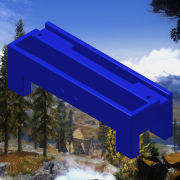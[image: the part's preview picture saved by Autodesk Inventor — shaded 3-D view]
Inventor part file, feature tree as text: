
AUTODESK INVENTOR PART (.ipt)
format: ipt  version: 2015 SP1 (Build 190203100, 203)  size: 321,536 bytes
history: native  units: in
note: dims shown in document units (in); Inventor stores cm internally (conversion verified against a paired STEP export)
features: sketch x11, extrude x7, hole x3, reference x2, fillet x1, projected_geometry x1
ambient origin geometry x8: Origin, YZ Plane, XZ Plane, XY Plane, X Axis, Y Axis, Z Axis, Center Point
bodies: Solid1 (feature_tree)
feature tree (25):
  extrude  "Extrusion1"  Depth=1.25in
  extrude  "Extrusion2"  Depth=2.5in TaperAngle=0.0deg
  extrude  "Extrusion3"  Depth=1.0in
  extrude  "Extrusion4"  Depth=1.0in
  extrude  "Extrusion5"  Depth=0.5in
  extrude  "Extrusion6"  Depth=0.5in
  sketch  "Sketch9"  dims[d13=1.0in d14=0.0in d15=3.8in]
  hole  "Hole1"  [1 undecoded]
  hole  "Hole2"  [1 undecoded]
  extrude  "Extrusion7"  Depth=7.0in
  hole  "Hole3"  [1 undecoded]
  fillet  "Fillet1"  Radius=0.75in
  sketch  "Sketch1"  dims[d0=7.5in d1=1.25in]
  sketch  "Sketch3"  dims[d2=7.5in d3=2.5in d4=0.0in]
  sketch  "Sketch4"  dims[d5=1.0in d6=1.0in]
  sketch  "Sketch5"  dims[d7=1.0in d8=1.0in]
  sketch  "Sketch6"  dims[d9=0.5in d10=0.5in]
  sketch  "Sketch8"  dims[d11=0.5in d12=0.5in]
  sketch  "Sketch10"  dims[d16=1.85in d17=1.0in d18=0.0in]
  reference  "Reference1"
  sketch  "Sketch11"  dims[d22=1.0in d23=0.0in d24=7.0in]
  reference  "Reference2"
  sketch  "Sketch12"  dims[d26=1.0in d27=0.0in d28=0.5in d29=0.75in]
  sketch  "Sketch13"  dims[d30=3.125in d34=0.525in d35=1.125in d36=2.9375in d37=0.211in d38=1.0in d39=0.0in d40=1.0in d41=0.25in d42=0.25in d43=0.1693in d44=0.75in d45=0.375in d46=0.25in d47=0.5635in d48=1.0in d49=0.8108in d50=0.25in d51=0.126in d52=0.75in d53=0.375in d54=0.25in d55=0.5635in d56=0.5in d57=0.8108in d58=0.25in d59=7.5in d60=0.0in d74=0.5in d75=0.25in d76=0.5in d77=0.25in d78=0.201in d79=0.75in d80=0.385in d81=0.25in d82=0.5635in d83=1.0in d84=0.8108in d85=0.0625in]
  projected_geometry  "Projected Loop1"
note: 3 required parameter values undecoded (feature->parameter linkage not recoverable at this tier; creation-order binding heuristic only, values carry confidence <= 0.55)
